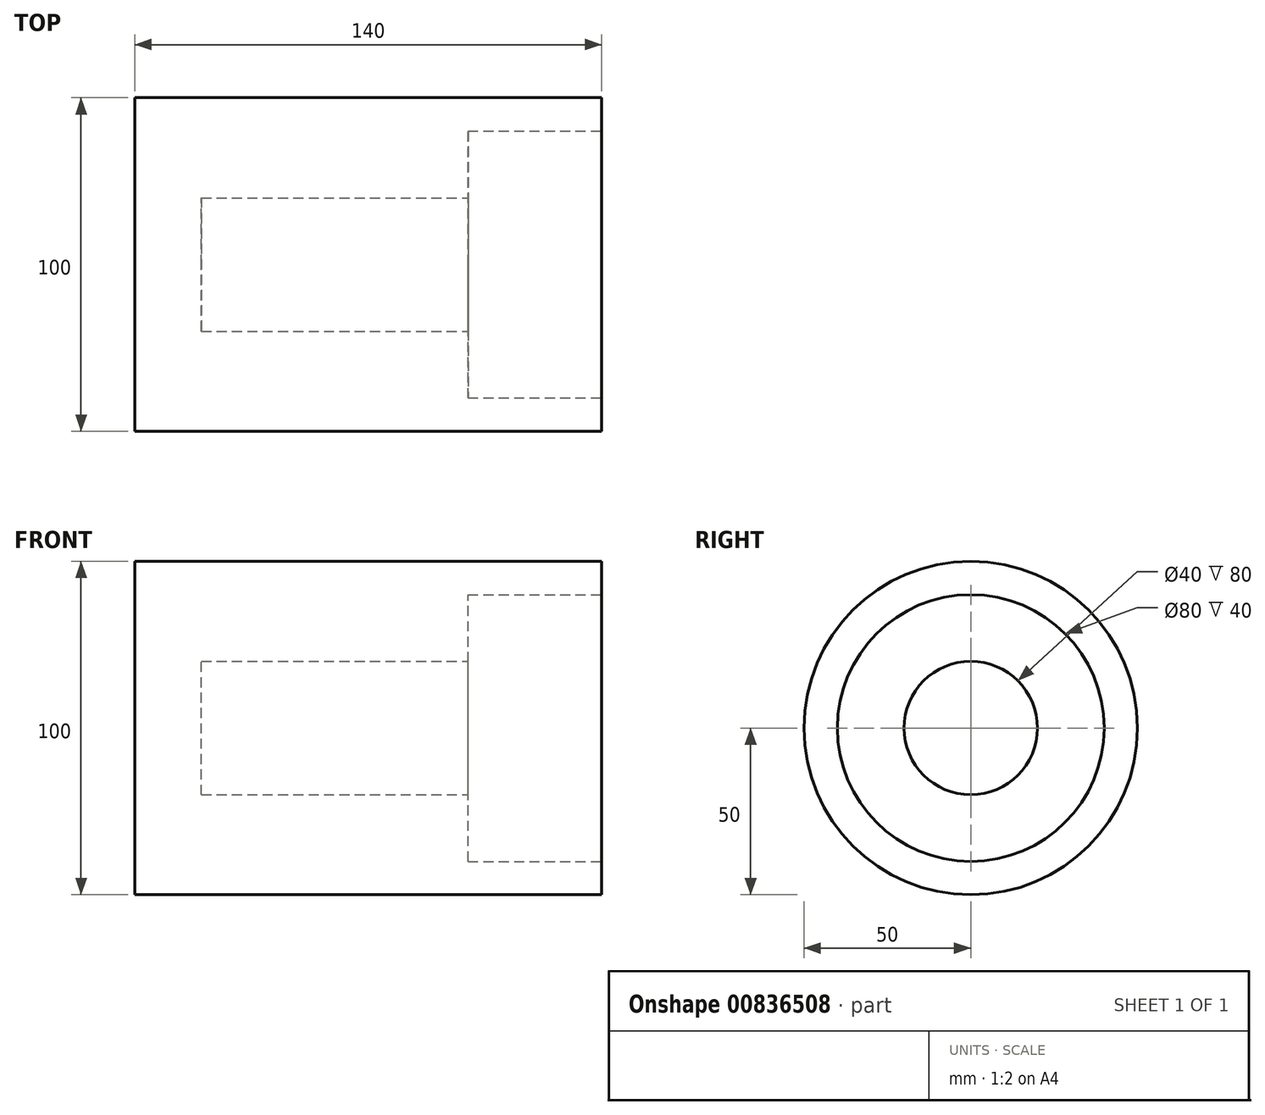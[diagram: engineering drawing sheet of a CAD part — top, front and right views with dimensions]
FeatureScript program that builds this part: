
annotation { "Feature Type Name" : "Feature", "Feature Type Description" : "" }
export const myFeature = defineFeature(function(context is Context, id is Id, definition is map)
    precondition{}
    {
        {
            var Q0;
            Q0=qCreatedBy(makeId("Front.planeOp"),FACE);
            var sketch = newSketch(context, id + "F0", { "sketchPlane" : qUnion([Q0])});
            skLineSegment(sketch, "E0", {"start": v(-140, 0) * mm, "end": v(-140, 50) * mm});
            skLineSegment(sketch, "E1", {"start": v(-140, 50) * mm, "end": v(0, 50) * mm});
            skLineSegment(sketch, "E2", {"start": v(0, 50) * mm, "end": v(0, 40) * mm});
            skLineSegment(sketch, "E3", {"start": v(0, 40) * mm, "end": v(-40, 40) * mm});
            skLineSegment(sketch, "E4", {"start": v(-40, 40) * mm, "end": v(-40, 20) * mm});
            skLineSegment(sketch, "E5", {"start": v(-40, 20) * mm, "end": v(-120, 20) * mm});
            skLineSegment(sketch, "E6", {"start": v(-120, 20) * mm, "end": v(-120, 0) * mm});
            skLineSegment(sketch, "E7", {"start": v(-120, 0) * mm, "end": v(-140, 0) * mm});
            skSolve(sketch);
        }
        {
            var Q0;
            Q0=makeQuery(id+"F0.imprint","IMPRINT",FACE,{"disambiguationData":[TD([[makeQuery(id+"F0.imprint","IMPRINT",EDGE,{"derivedFrom":sQuery(id+"F0.wireOp",EDGE,"E0")}),-1.0]])]});
            var Q1;
            Q1=sQuery(id+"F0.wireOp",EDGE,"E7");
            revolve(context, id + "F1", {"surfaceOperationType" : NewSurfaceOperationType.NEW, "entities" : qUnion([Q0]), "axis" : qUnion([Q1]), "revolveType" : RevolveType.FULL});
        }
    });
